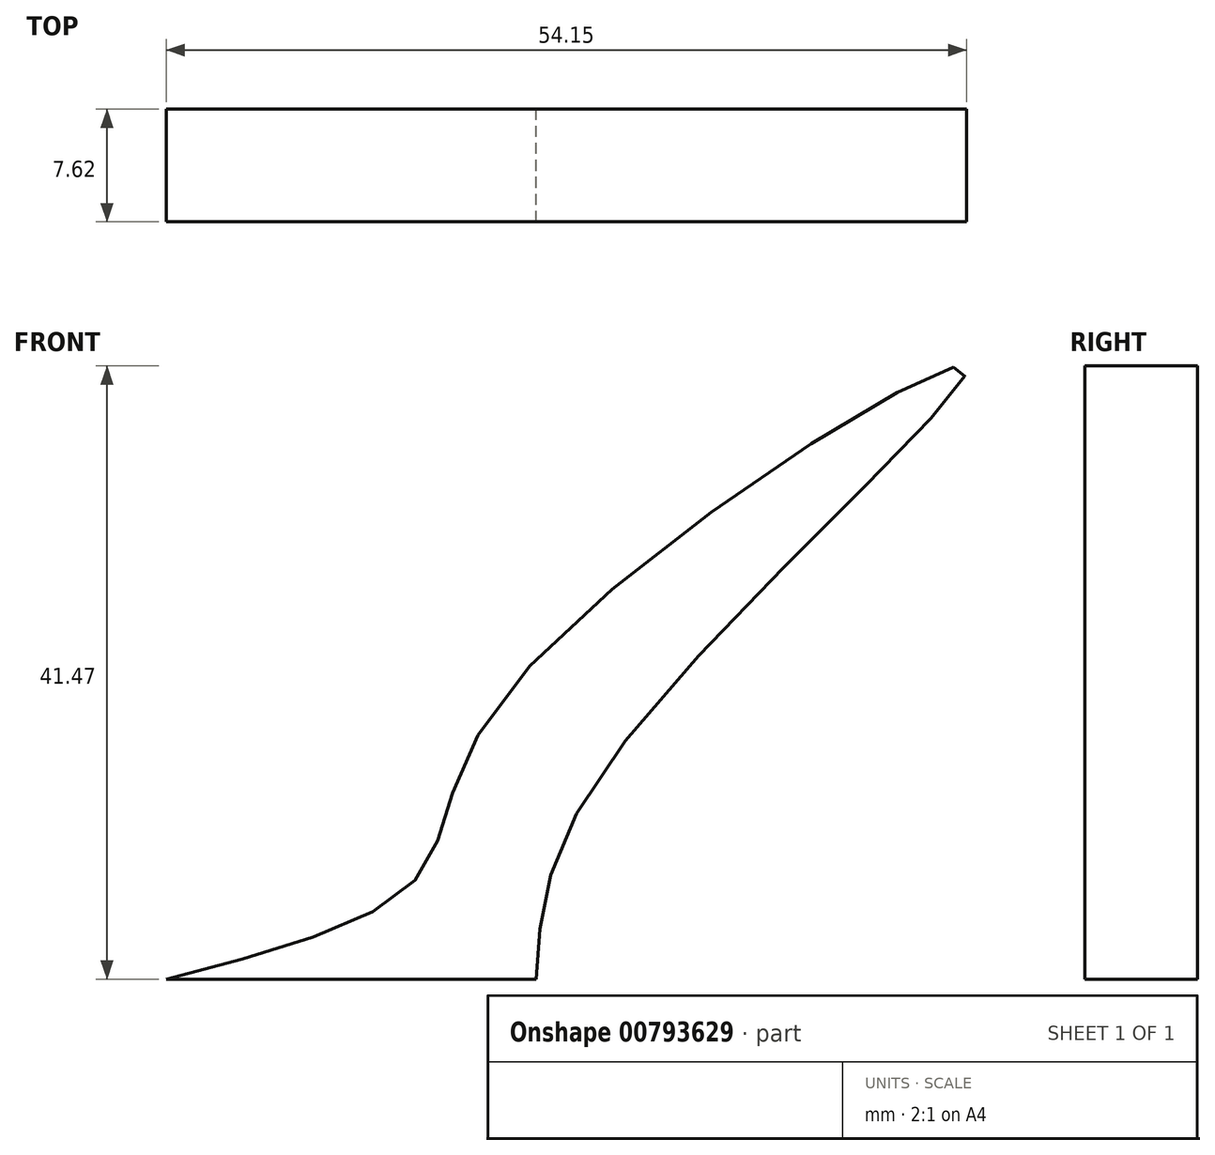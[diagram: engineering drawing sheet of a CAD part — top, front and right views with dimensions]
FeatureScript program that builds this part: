
annotation { "Feature Type Name" : "Feature", "Feature Type Description" : "" }
export const myFeature = defineFeature(function(context is Context, id is Id, definition is map)
    precondition{}
    {
        {
            var Q0;
            Q0=qCreatedBy(makeId("Front.planeOp"),FACE);
            var sketch = newSketch(context, id + "F0", { "sketchPlane" : qUnion([Q0])});
            skFitSpline(sketch, "E0", {"points": [v(6.48, 7.66) * mm, v(23.5, 14.56) * mm, v(29.47, 26.96) * mm, v(60.55, 49.06) * mm, v(36.83, 22.84) * mm, v(31.53, 7.66) * mm], "startDerivative": vector(120.4, 30.55) * mm, "endDerivative": vector(-3.26, -76.8) * mm});
            skLineSegment(sketch, "E1", {"start": v(6.48, 7.66) * mm, "end": v(31.53, 7.66) * mm});
            skSolve(sketch);
        }
        {
            var Q0;
            Q0 = qSketchRegion(id + "F0", true);
            extrude(context, id + "F1", {"entities" : qUnion([Q0]), "depth" : 7.62 * mm, "offsetDistance" : 25.4 * mm});
        }
    });
